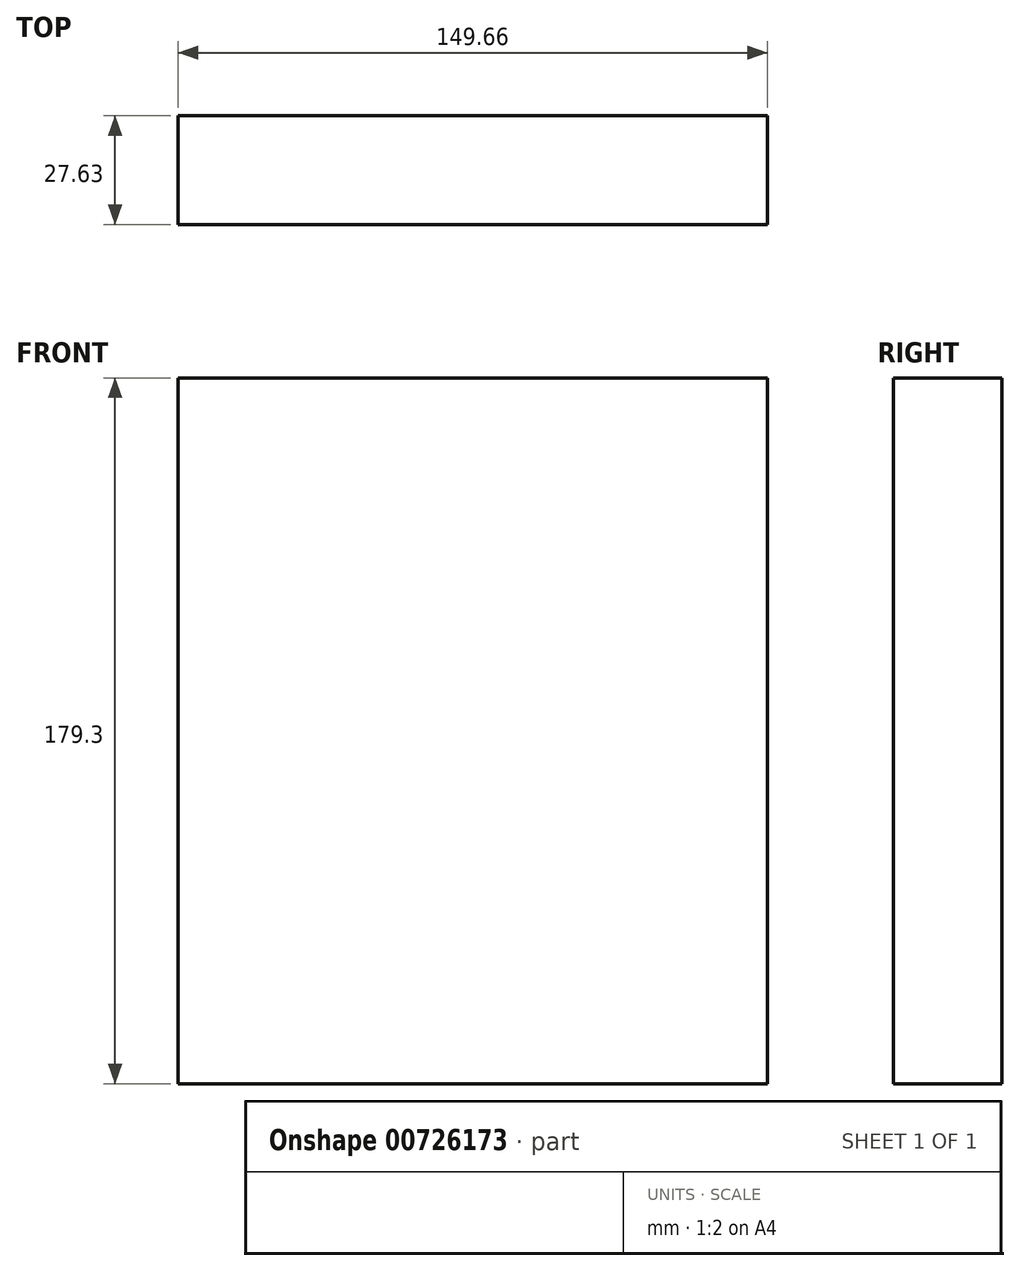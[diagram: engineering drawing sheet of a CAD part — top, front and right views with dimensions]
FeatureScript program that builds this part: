
annotation { "Feature Type Name" : "Feature", "Feature Type Description" : "" }
export const myFeature = defineFeature(function(context is Context, id is Id, definition is map)
    precondition{}
    {
        {
            var Q0;
            Q0=qCreatedBy(makeId("Top.planeOp"),FACE);
            var sketch = newSketch(context, id + "F0", { "sketchPlane" : qUnion([Q0])});
            skLineSegment(sketch, "E0.bottom", {"start": v(-74.4, 74.97) * mm, "end": v(75.26, 74.97) * mm});
            skLineSegment(sketch, "E0.top", {"start": v(-74.4, 47.34) * mm, "end": v(75.26, 47.34) * mm});
            skLineSegment(sketch, "E0.left", {"start": v(-74.4, 74.97) * mm, "end": v(-74.4, 47.34) * mm});
            skLineSegment(sketch, "E0.right", {"start": v(75.26, 74.97) * mm, "end": v(75.26, 47.34) * mm});
            skSolve(sketch);
        }
        {
            var Q0;
            Q0=makeQuery(id+"F0.imprint","IMPRINT",FACE,{"disambiguationData":[TD([[makeQuery(id+"F0.imprint","IMPRINT",EDGE,{"derivedFrom":sQuery(id+"F0.wireOp",EDGE,"E0.bottom")}),-1.0]])]});
            extrude(context, id + "F1", {"entities" : qUnion([Q0]), "oppositeDirection" : true, "depth" : 179.3 * mm, "offsetDistance" : 25 * mm});
        }
    });
